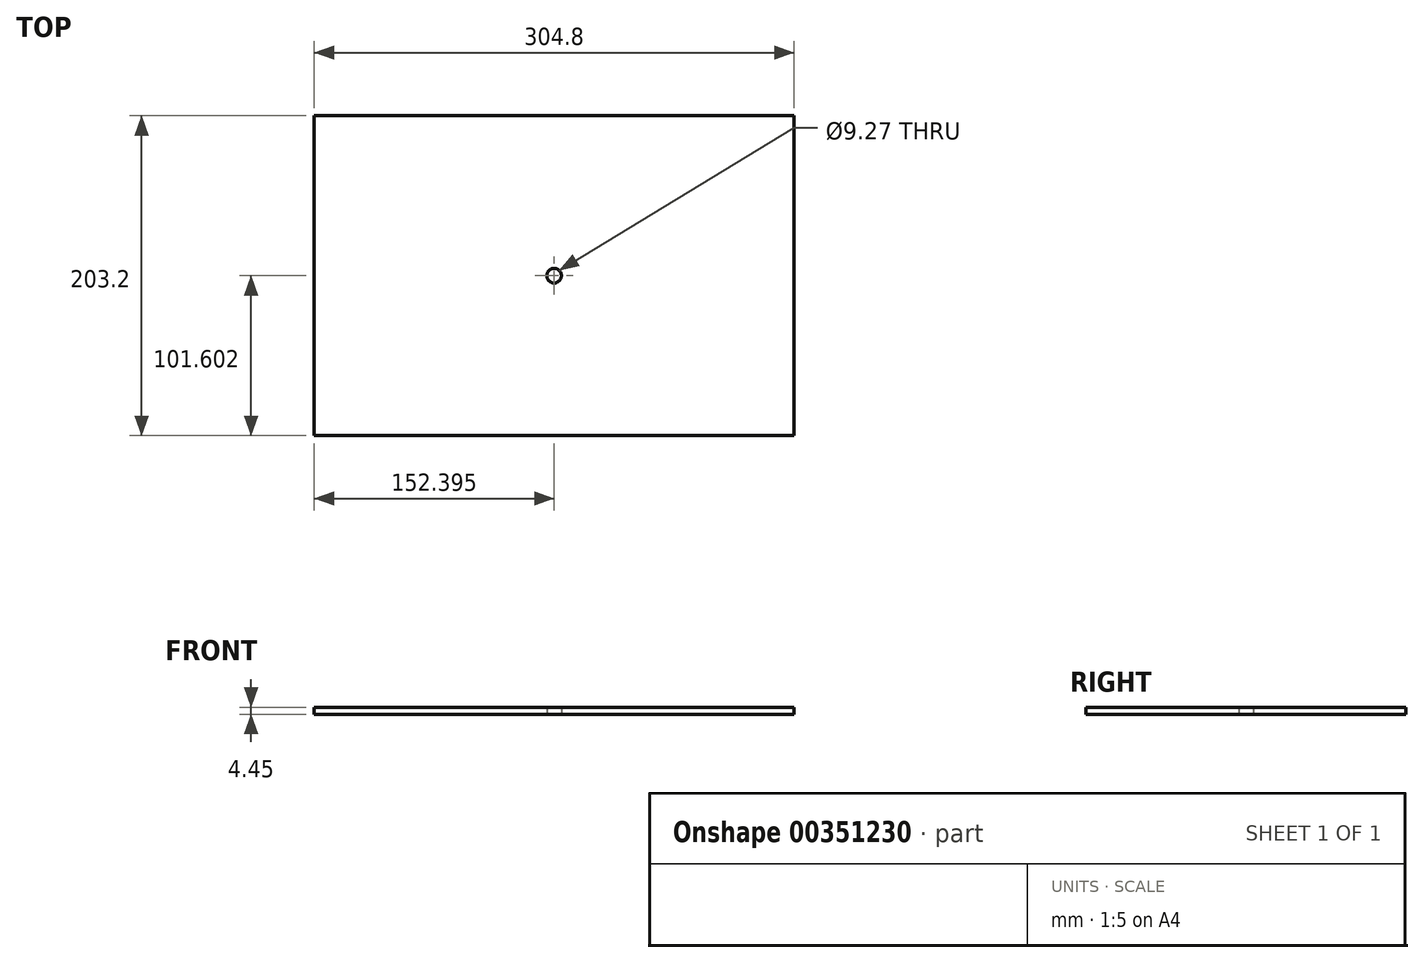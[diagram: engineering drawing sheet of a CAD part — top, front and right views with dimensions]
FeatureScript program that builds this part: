
annotation { "Feature Type Name" : "Feature", "Feature Type Description" : "" }
export const myFeature = defineFeature(function(context is Context, id is Id, definition is map)
    precondition{}
    {
        {
            var Q0;
            Q0=qCreatedBy(makeId("Top.planeOp"),FACE);
            var sketch = newSketch(context, id + "F0", { "sketchPlane" : qUnion([Q0])});
            skLineSegment(sketch, "E0.bottom", {"start": v(-65.73, 170.5) * mm, "end": v(239.07, 170.5) * mm});
            skLineSegment(sketch, "E0.top", {"start": v(-65.73, -32.7) * mm, "end": v(239.07, -32.7) * mm});
            skLineSegment(sketch, "E0.left", {"start": v(-65.73, 170.5) * mm, "end": v(-65.73, -32.7) * mm});
            skLineSegment(sketch, "E0.right", {"start": v(239.07, 170.5) * mm, "end": v(239.07, -32.7) * mm});
            skCircle(sketch, "E1", {"center": v(86.67, 68.9) * mm, "radius": 4.64 * mm});
            skSolve(sketch);
        }
        {
            var Q0;
            Q0 = qSketchRegion(id + "F0", true);
            extrude(context, id + "F1", {"entities" : qUnion([Q0]), "depth" : 4.44 * mm});
        }
    });
